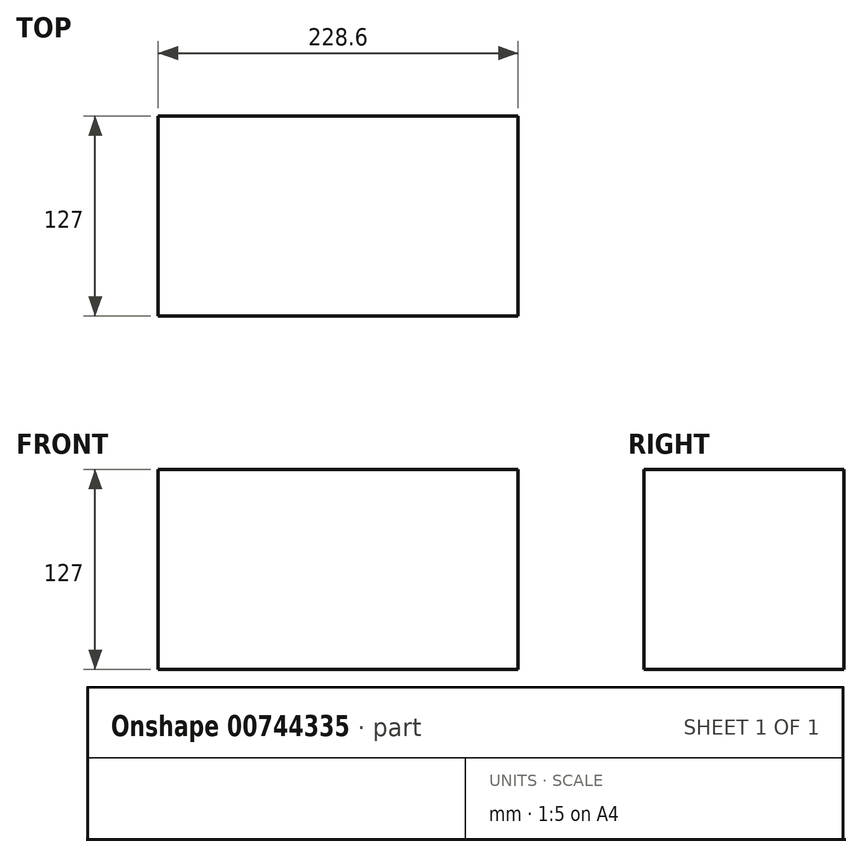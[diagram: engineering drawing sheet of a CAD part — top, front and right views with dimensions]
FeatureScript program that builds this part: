
annotation { "Feature Type Name" : "Feature", "Feature Type Description" : "" }
export const myFeature = defineFeature(function(context is Context, id is Id, definition is map)
    precondition{}
    {
        {
            var Q0;
            Q0=qCreatedBy(makeId("Top.planeOp"),FACE);
            var sketch = newSketch(context, id + "F0", { "sketchPlane" : qUnion([Q0])});
            skLineSegment(sketch, "E0.bottom", {"start": v(0, 0) * mm, "end": v(-228.6, 0) * mm});
            skLineSegment(sketch, "E0.top", {"start": v(0, 127) * mm, "end": v(-228.6, 127) * mm});
            skLineSegment(sketch, "E0.left", {"start": v(0, 0) * mm, "end": v(0, 127) * mm});
            skLineSegment(sketch, "E0.right", {"start": v(-228.6, 0) * mm, "end": v(-228.6, 127) * mm});
            skSolve(sketch);
        }
        {
            var Q0;
            Q0=makeQuery(id+"F0.imprint","IMPRINT",FACE,{"disambiguationData":[TD([[makeQuery(id+"F0.imprint","IMPRINT",EDGE,{"derivedFrom":sQuery(id+"F0.wireOp",EDGE,"E0.bottom")}),-1.0]])]});
            extrude(context, id + "F1", {"entities" : qUnion([Q0]), "depth" : 127 * mm, "offsetDistance" : 25.4 * mm});
        }
    });
